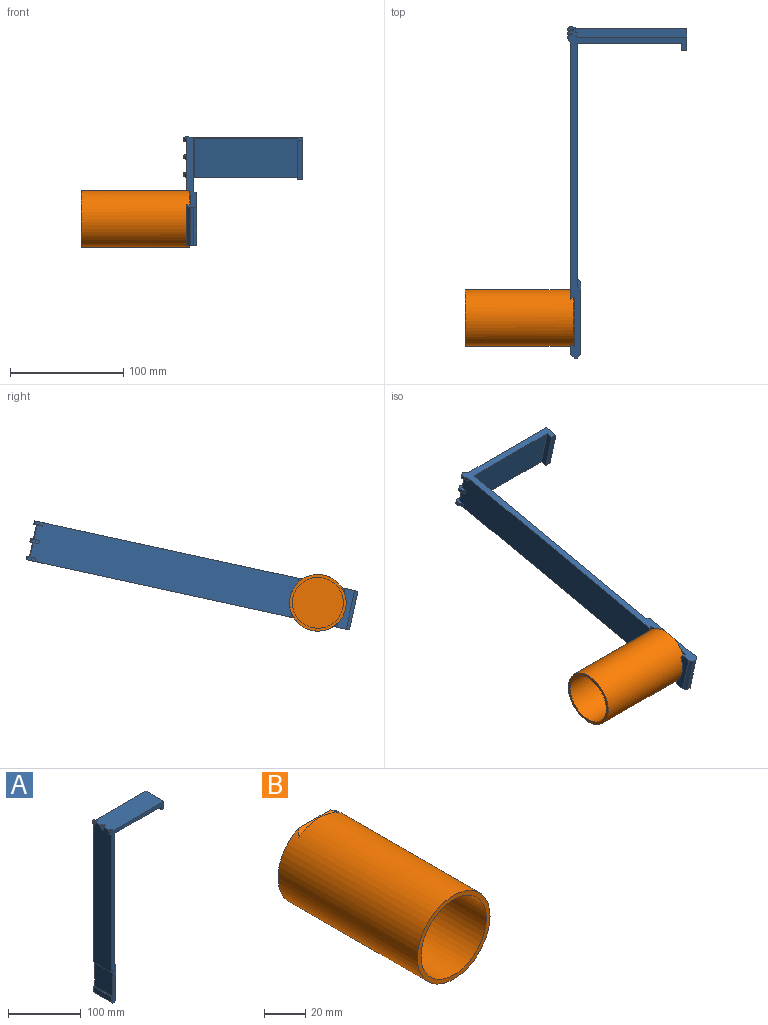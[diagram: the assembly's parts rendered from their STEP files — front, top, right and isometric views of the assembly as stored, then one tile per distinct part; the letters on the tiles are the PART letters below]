
ASSEMBLY  parts=2 mates=1
PART A: 36 faces, bbox 105x35x292.5 mm
  f0: plane 236.23x35mm, normal (-1,0,0), area 8221.9mm2, adj f1,f2,f5,f6,f15,f23,f26,f27
  f1: cylinder r=0.5mm len=13mm, axis (0,-1,0), area 10.2mm2, adj f0,f8,f30,f35
  f2: cylinder r=0.5mm len=13mm, axis (0,-1,0), area 10.2mm2, adj f0,f8,f26,f31
  f3: plane 219.2x35mm, normal (1,0,0), area 7671.9mm2, adj f5,f6,f18,f22
  f4: plane 35x8.73mm, normal (-1,0,0), area 305.6mm2, adj f5,f6,f14,f19
  f5: plane 292.5x105mm, normal (0,-1,0), area 2420.6mm2, adj f0,f3,f4,f7,f8,f9,f10,f11
  f6: plane 292.5x105mm, normal (0,1,0), area 2420.6mm2, adj f0,f3,f4,f7,f8,f9,f10,f11
  f7: plane 35x3mm, normal (0,0,-1), area 105mm2, adj f5,f6,f17,f19
  f8: plane 102x35mm, normal (0,0,1), area 3523.8mm2, adj f1,f2,f5,f6,f12,f25,f26,f29
  f9: plane 91x35mm, normal (0,0,-1), area 3185mm2, adj f5,f6,f10,f22
  f10: plane 35x6mm, normal (-1,0,0), area 210mm2, adj f5,f6,f9,f11
  f11: plane 35x5mm, normal (0,0,-1), area 175mm2, adj f5,f6,f10,f12
  f12: plane 35x12mm, normal (1,0,0), area 420mm2, adj f5,f6,f8,f11
  f13: plane 43.27x35mm, normal (-1,0,0), area 1514.4mm2, adj f5,f6,f20,f21
  f14: plane 35x2.25mm, normal (0.5,0,0.87), area 90.9mm2, adj f4,f5,f6,f21
  f15: plane 35x2.25mm, normal (0.5,0,-0.87), area 90.9mm2, adj f0,f5,f6,f20
  f16: plane 58.3x35mm, normal (1,0,0), area 2040.6mm2, adj f5,f6,f17,f18
  f17: plane 35x3mm, normal (0.71,0,-0.71), area 148.5mm2, adj f5,f6,f7,f16
  f18: plane 35x3mm, normal (0.71,0,0.71), area 148.5mm2, adj f3,f5,f6,f16
  f19: plane 35x3mm, normal (-0.71,0,-0.71), area 148.5mm2, adj f4,f5,f6,f7
  f20: cylinder r=0.5mm len=35mm, axis (0,1,0), area 36.7mm2, adj f5,f6,f13,f15
  f21: cylinder r=0.5mm len=35mm, axis (0,1,0), area 36.7mm2, adj f5,f6,f13,f14
  f22: cylinder r=0.5mm len=35mm, axis (0,1,0), area 27.5mm2, adj f3,f5,f6,f9
  f23: plane 3.63x3mm, normal (-0.87,0,-0.5), area 12.6mm2, adj f0,f6,f24,f26
  f24: cylinder r=3mm len=4.5mm, axis (0,1,0), area 23.6mm2, adj f6,f23,f25,f26
  f25: plane 3.63x3mm, normal (0.5,0,0.87), area 12.6mm2, adj f6,f8,f24,f26
  f26: plane 8.13x8.13mm, normal (0,-1,0), area 21.6mm2, adj f0,f2,f8,f23,f24,f25
  f27: plane 3.63x3mm, normal (-0.87,0,-0.5), area 12.6mm2, adj f0,f28,f30,f31
  f28: cylinder r=3mm len=4.5mm, axis (0,1,0), area 23.6mm2, adj f27,f29,f30,f31
  f29: plane 3.63x3mm, normal (0.5,0,0.87), area 12.6mm2, adj f8,f28,f30,f31
  f30: plane 8.13x8.13mm, normal (0,-1,0), area 21.6mm2, adj f0,f1,f8,f27,f28,f29
  f31: plane 8.13x8.13mm, normal (0,1,0), area 21.6mm2, adj f0,f2,f8,f27,f28,f29
  f32: plane 3.63x3mm, normal (-0.87,0,-0.5), area 12.6mm2, adj f0,f5,f33,f35
  f33: cylinder r=3mm len=4.5mm, axis (0,1,0), area 23.6mm2, adj f5,f32,f34,f35
  f34: plane 3.63x3mm, normal (0.5,0,0.87), area 12.6mm2, adj f5,f8,f33,f35
  f35: plane 8.13x8.13mm, normal (0,1,0), area 21.6mm2, adj f0,f1,f8,f32,f33,f34
PART B: 9 faces, bbox 50x96x50 mm
  f0: cylinder r=25mm len=96mm, axis (0,1,0), area 14901.9mm2, adj f1,f2,f5,f6,f7,f8
  f1: plane 50x44.9mm, normal (0,1,0), area 1887.9mm2, adj f0,f6,f8
  f2: plane 50x50mm, normal (0,-1,0), area 373.1mm2, adj f0,f3
  f3: cylinder r=22.5mm len=87.5mm, axis (0,1,0), area 12370mm2, adj f2,f4
  f4: plane 45x45mm, normal (0,-1,0), area 1590.4mm2, adj f3
  f5: plane 28.53x4.47mm, normal (0,1,0), area 86.7mm2, adj f0,f6
  f6: plane 28.53x3.32mm, normal (0,-0.5,-0.87), area 97.7mm2, adj f0,f1,f5
  f7: plane 28.53x4.47mm, normal (0,1,0), area 86.7mm2, adj f0,f8
  f8: plane 28.53x3.32mm, normal (0,-0.5,0.87), area 97.7mm2, adj f0,f1,f7
PLACE A rot(axis=(-1,0,0),77.7deg) t=(-20.63,97.97,-21.49)mm
PLACE B rot(axis=(0.61,0.61,-0.5),127.3deg) t=(-26.77,10.17,-39.71)mm
MATE pin_slot B.f6 <-> A.f15  axis (-0.5,0.85,0.18) through (-22.5,31.13,-35.15)mm
